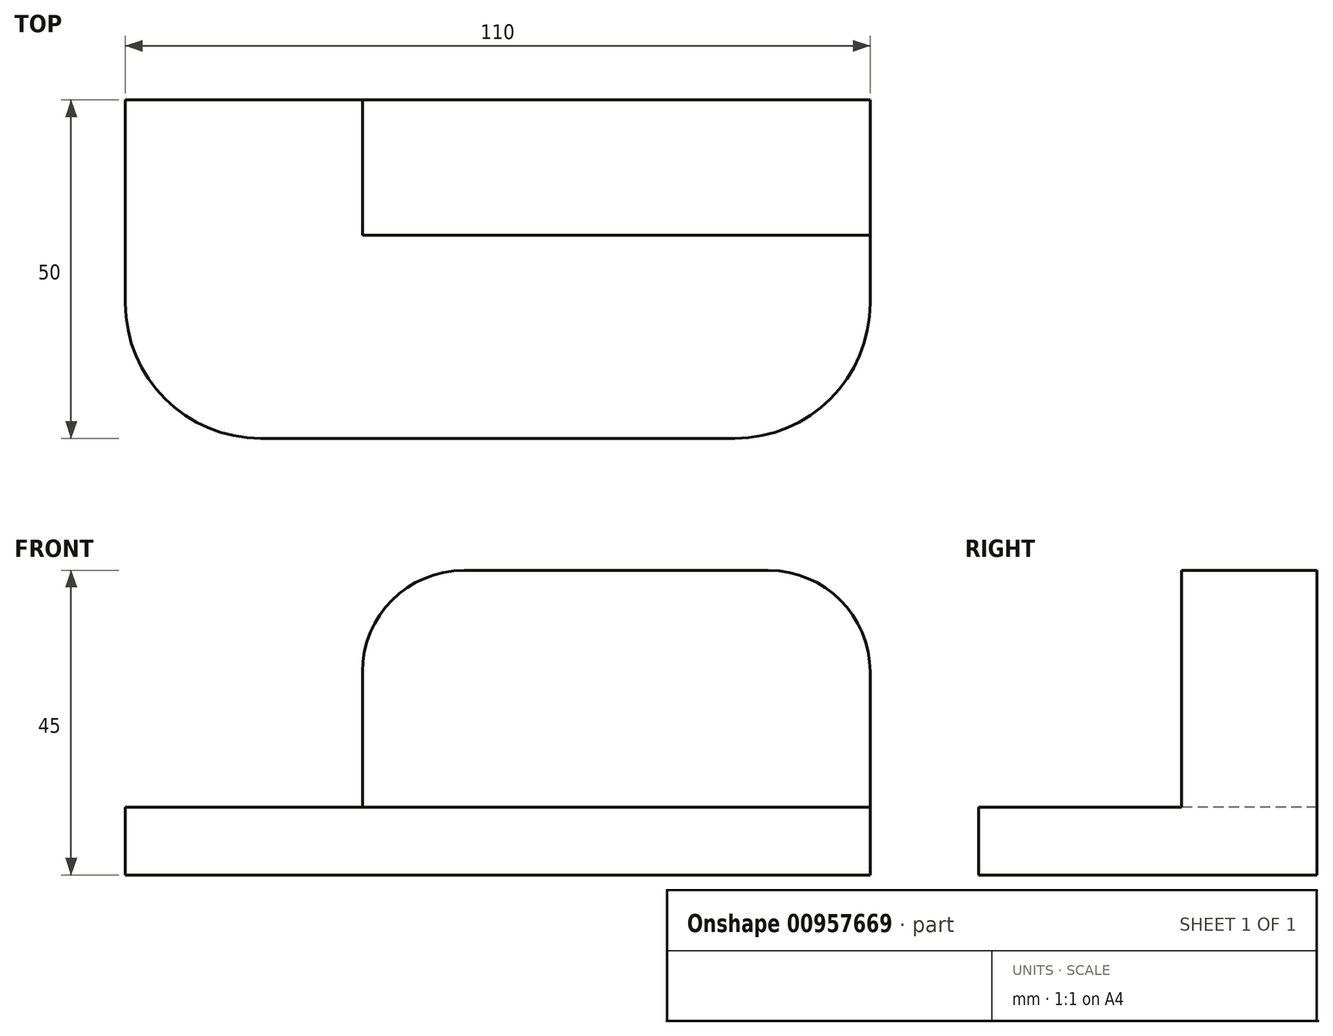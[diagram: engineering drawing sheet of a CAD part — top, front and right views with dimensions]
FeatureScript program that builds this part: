
annotation { "Feature Type Name" : "Feature", "Feature Type Description" : "" }
export const myFeature = defineFeature(function(context is Context, id is Id, definition is map)
    precondition{}
    {
        {
            var Q0;
            Q0=qCreatedBy(makeId("Top.planeOp"),FACE);
            var sketch = newSketch(context, id + "F0", { "sketchPlane" : qUnion([Q0])});
            skLineSegment(sketch, "E0.bottom", {"start": v(0, 0) * mm, "end": v(110, 0) * mm});
            skLineSegment(sketch, "E0.top", {"start": v(0, -50) * mm, "end": v(110, -50) * mm});
            skLineSegment(sketch, "E0.left", {"start": v(0, 0) * mm, "end": v(0, -50) * mm});
            skLineSegment(sketch, "E0.right", {"start": v(110, 0) * mm, "end": v(110, -50) * mm});
            skSolve(sketch);
        }
        {
            var Q0;
            Q0=makeQuery(id+"F0.imprint","IMPRINT",FACE,{"disambiguationData":[TD([[makeQuery(id+"F0.imprint","IMPRINT",EDGE,{"derivedFrom":sQuery(id+"F0.wireOp",EDGE,"E0.bottom")}),-1.0]])]});
            extrude(context, id + "F1", {"entities" : qUnion([Q0]), "depth" : 10 * mm, "offsetDistance" : 25 * mm});
        }
        {
            var Q0;
            Q0=makeQuery(id+"F1.opExtrude","SWEPT_EDGE",EDGE,{"disambiguationData":[OSD([sQuery(id+"F0.wireOp",EDGE,"E0.top"),sQuery(id+"F0.wireOp",EDGE,"E0.left")])]});
            var Q1;
            Q1=makeQuery(id+"F1.opExtrude","SWEPT_EDGE",EDGE,{"disambiguationData":[OSD([sQuery(id+"F0.wireOp",EDGE,"E0.top"),sQuery(id+"F0.wireOp",EDGE,"E0.right")])]});
            fillet(context, id + "F2", {"entities" : qUnion([Q0, Q1]), "radius" : 20 * mm, "tangentPropagation" : true, "allowEdgeOverflow" : false});
        }
        {
            var Q0;
            Q0=makeQuery(id+"F1.opExtrude","CAP_FACE",FACE,{"disambiguationData":[OSD([sQuery(id+"F0.wireOp",EDGE,"E0.bottom"),sQuery(id+"F0.wireOp",EDGE,"E0.top"),sQuery(id+"F0.wireOp",EDGE,"E0.left"),sQuery(id+"F0.wireOp",EDGE,"E0.right")])],"isStart":false});
            var sketch = newSketch(context, id + "F3", { "sketchPlane" : qUnion([Q0])});
            skLineSegment(sketch, "E1.bottom", {"start": v(110, 0) * mm, "end": v(35, 0) * mm});
            skLineSegment(sketch, "E1.top", {"start": v(110, -20) * mm, "end": v(35, -20) * mm});
            skLineSegment(sketch, "E1.left", {"start": v(110, 0) * mm, "end": v(110, -20) * mm});
            skLineSegment(sketch, "E1.right", {"start": v(35, 0) * mm, "end": v(35, -20) * mm});
            skSolve(sketch);
        }
        {
            var Q0;
            Q0=makeQuery(id+"F3.imprint","IMPRINT",FACE,{"disambiguationData":[TD([[makeQuery(id+"F3.imprint","IMPRINT",EDGE,{"derivedFrom":sQuery(id+"F3.wireOp",EDGE,"E1.bottom")}),-1.0]])]});
            extrude(context, id + "F4", {"entities" : qUnion([Q0]), "operationType" : NewBodyOperationType.ADD, "depth" : 35 * mm, "offsetDistance" : 25 * mm});
        }
        {
            var Q0;
            Q0=makeQuery(id+"F4.opExtrude","CAP_EDGE",EDGE,{"disambiguationData":[OSD([sQuery(id+"F3.wireOp",EDGE,"E1.right")])],"isStart":false});
            var Q1;
            Q1=makeQuery(id+"F4.opExtrude","CAP_EDGE",EDGE,{"disambiguationData":[OSD([sQuery(id+"F3.wireOp",EDGE,"E1.left")])],"isStart":false});
            fillet(context, id + "F5", {"entities" : qUnion([Q0, Q1]), "radius" : 15 * mm, "tangentPropagation" : true, "allowEdgeOverflow" : false});
        }
    });
